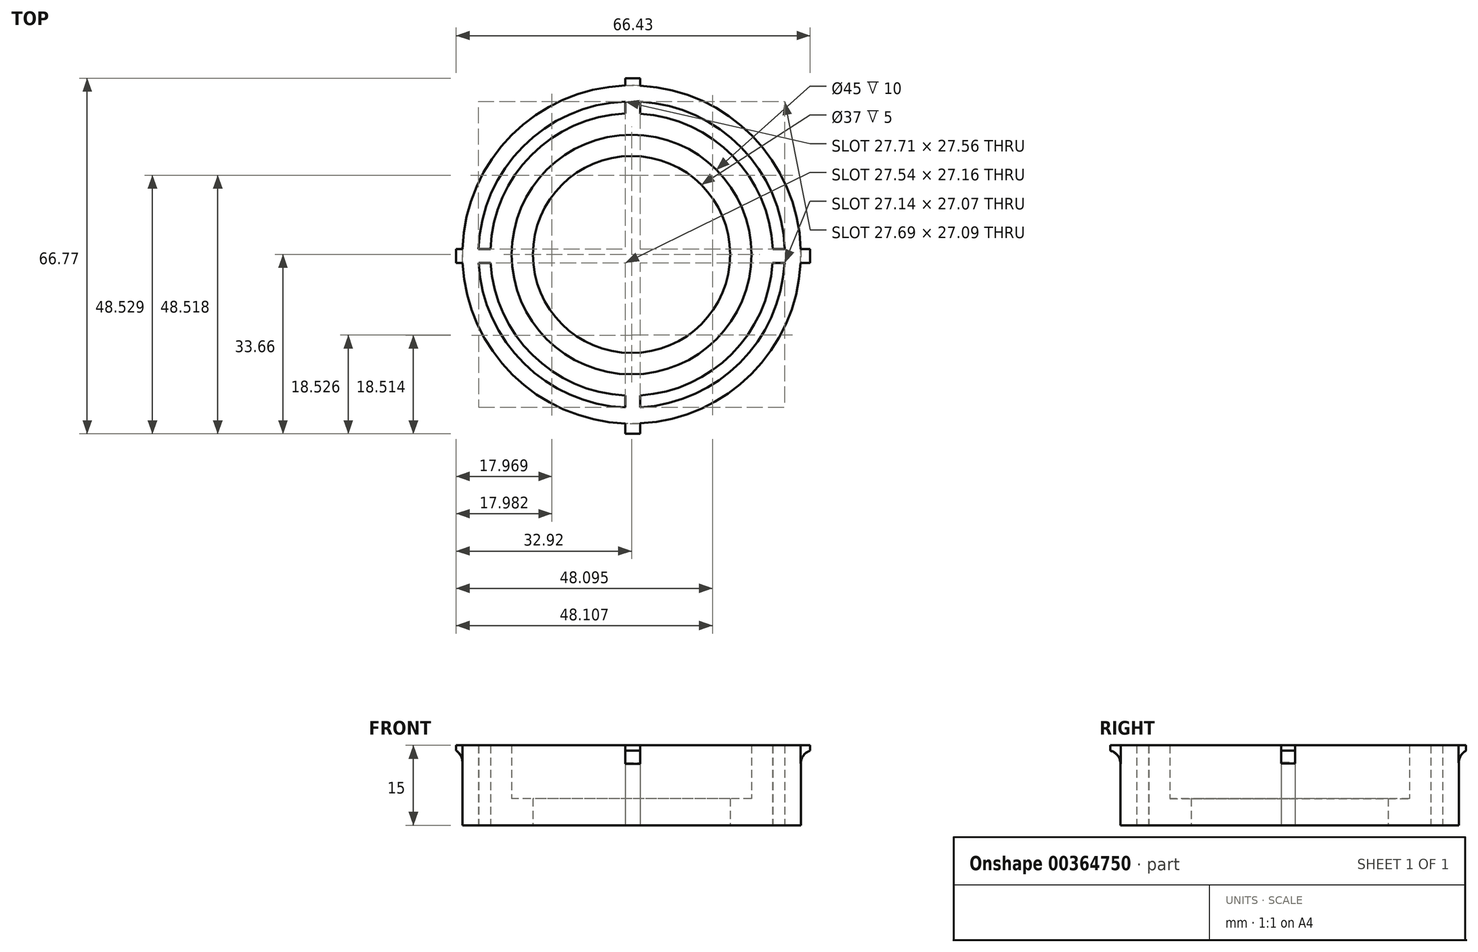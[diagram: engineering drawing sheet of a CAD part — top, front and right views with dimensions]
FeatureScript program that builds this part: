
annotation { "Feature Type Name" : "Feature", "Feature Type Description" : "" }
export const myFeature = defineFeature(function(context is Context, id is Id, definition is map)
    precondition{}
    {
        {
            var Q0;
            Q0=qCreatedBy(makeId("Top.planeOp"),FACE);
            var sketch = newSketch(context, id + "F0", { "sketchPlane" : qUnion([Q0])});
            skCircle(sketch, "E0", {"center": v(0, 0) * mm, "radius": 18.5 * mm});
            skCircle(sketch, "E1.0", {"center": v(0, 0) * mm, "radius": 22.5 * mm});
            skCircle(sketch, "E2.0", {"center": v(0, 0) * mm, "radius": 26.5 * mm});
            skLineSegment(sketch, "E3.bottom", {"start": v(-32.92, 1.01) * mm, "end": v(-24.48, 1.01) * mm});
            skLineSegment(sketch, "E3.top", {"start": v(-32.92, -1.56) * mm, "end": v(-24.48, -1.56) * mm});
            skLineSegment(sketch, "E3.left", {"start": v(-32.92, 1.01) * mm, "end": v(-32.92, -1.56) * mm});
            skLineSegment(sketch, "E3.right", {"start": v(-24.48, 1.01) * mm, "end": v(-24.48, -1.56) * mm});
            skLineSegment(sketch, "E4.bottom", {"start": v(-1.17, 33.11) * mm, "end": v(1.64, 33.11) * mm});
            skLineSegment(sketch, "E4.top", {"start": v(-1.17, 24.56) * mm, "end": v(1.64, 24.56) * mm});
            skLineSegment(sketch, "E4.left", {"start": v(-1.17, 33.11) * mm, "end": v(-1.17, 24.56) * mm});
            skLineSegment(sketch, "E4.right", {"start": v(1.64, 33.11) * mm, "end": v(1.64, 24.56) * mm});
            skLineSegment(sketch, "E5.bottom", {"start": v(33.5, -1.56) * mm, "end": v(24.13, -1.56) * mm});
            skLineSegment(sketch, "E5.top", {"start": v(33.5, 1.01) * mm, "end": v(24.13, 1.01) * mm});
            skLineSegment(sketch, "E5.left", {"start": v(33.5, -1.56) * mm, "end": v(33.5, 1.01) * mm});
            skLineSegment(sketch, "E5.right", {"start": v(24.13, -1.56) * mm, "end": v(24.13, 1.01) * mm});
            skLineSegment(sketch, "E6.bottom", {"start": v(-1.17, -25) * mm, "end": v(1.64, -25) * mm});
            skLineSegment(sketch, "E6.top", {"start": v(-1.17, -33.66) * mm, "end": v(1.64, -33.66) * mm});
            skLineSegment(sketch, "E6.left", {"start": v(-1.17, -25) * mm, "end": v(-1.17, -33.66) * mm});
            skLineSegment(sketch, "E6.right", {"start": v(1.64, -25) * mm, "end": v(1.64, -33.66) * mm});
            skCircle(sketch, "E7.0", {"center": v(0, 0) * mm, "radius": 31.75 * mm});
            skCircle(sketch, "E8.0", {"center": v(0, 0) * mm, "radius": 28.75 * mm});
            skCircle(sketch, "E9.0", {"center": v(0, 0) * mm, "radius": 34.75 * mm});
            skSolve(sketch);
        }
        {
            var Q0;
            Q0=makeQuery(id+"F0.imprint","IMPRINT",FACE,{"disambiguationData":[TD([[makeQuery(id+"F0.imprint","IMPRINT",EDGE,{"derivedFrom":sQuery(id+"F0.wireOp",EDGE,"E1.0")}),-1.0]])]});
            var Q1;
            {var subQ5=sQuery(id+"F0.wireOp",EDGE,"E6.bottom");Q1=makeQuery(id+"F0.imprint","IMPRINT",FACE,{"disambiguationData":[TD([[makeQuery(id+"F0.imprint","IMPRINT",EDGE,{"derivedFrom":subQ5}),-1.0]])]});}
            var Q2;
            {var subQ0=sQuery(id+"F0.wireOp",EDGE,"E6.left");var subQ1=sQuery(id+"F0.wireOp",EDGE,"E2.0");var subQ2=makeQuery(id+"F0.imprint","INTERSECT",VERTEX,{"derivedFrom":[subQ1,subQ0]});Q2=makeQuery(id+"F0.imprint","IMPRINT",FACE,{"disambiguationData":[TD([[makeQuery(id+"F0.imprint","IMPRINT",EDGE,{"disambiguationData":[TD([[subQ2,-1.0]])],"derivedFrom":subQ1}),-1.0]])]});}
            var Q3;
            {var subQ0=sQuery(id+"F0.wireOp",EDGE,"E7.0");var subQ1=sQuery(id+"F0.wireOp",EDGE,"E6.left");var subQ2=makeQuery(id+"F0.imprint","INTERSECT",VERTEX,{"derivedFrom":[subQ1,subQ0]});Q3=makeQuery(id+"F0.imprint","IMPRINT",FACE,{"disambiguationData":[TD([[makeQuery(id+"F0.imprint","IMPRINT",EDGE,{"disambiguationData":[TD([[subQ2,1.0]])],"derivedFrom":subQ1}),1.0]])]});}
            var Q4;
            {var subQ0=sQuery(id+"F0.wireOp",EDGE,"E7.0");var subQ1=sQuery(id+"F0.wireOp",EDGE,"E5.bottom");var subQ2=makeQuery(id+"F0.imprint","INTERSECT",VERTEX,{"derivedFrom":[subQ1,subQ0]});Q4=makeQuery(id+"F0.imprint","IMPRINT",FACE,{"disambiguationData":[TD([[makeQuery(id+"F0.imprint","IMPRINT",EDGE,{"disambiguationData":[TD([[subQ2,-1.0]])],"derivedFrom":subQ1}),1.0]])]});}
            var Q5;
            {var subQ0=sQuery(id+"F0.wireOp",EDGE,"E7.0");var subQ1=sQuery(id+"F0.wireOp",EDGE,"E5.bottom");var subQ2=makeQuery(id+"F0.imprint","INTERSECT",VERTEX,{"derivedFrom":[subQ1,subQ0]});Q5=makeQuery(id+"F0.imprint","IMPRINT",FACE,{"disambiguationData":[TD([[makeQuery(id+"F0.imprint","IMPRINT",EDGE,{"disambiguationData":[TD([[subQ2,-1.0]])],"derivedFrom":subQ1}),-1.0]])]});}
            var Q6;
            {var subQ0=sQuery(id+"F0.wireOp",EDGE,"E7.0");var subQ1=sQuery(id+"F0.wireOp",EDGE,"E4.right");var subQ2=makeQuery(id+"F0.imprint","INTERSECT",VERTEX,{"derivedFrom":[subQ1,subQ0]});Q6=makeQuery(id+"F0.imprint","IMPRINT",FACE,{"disambiguationData":[TD([[makeQuery(id+"F0.imprint","IMPRINT",EDGE,{"disambiguationData":[TD([[subQ2,-1.0]])],"derivedFrom":subQ1}),1.0]])]});}
            var Q7;
            {var subQ0=sQuery(id+"F0.wireOp",EDGE,"E5.top");var subQ1=sQuery(id+"F0.wireOp",EDGE,"E2.0");var subQ2=makeQuery(id+"F0.imprint","INTERSECT",VERTEX,{"derivedFrom":[subQ1,subQ0]});Q7=makeQuery(id+"F0.imprint","IMPRINT",FACE,{"disambiguationData":[TD([[makeQuery(id+"F0.imprint","IMPRINT",EDGE,{"disambiguationData":[TD([[subQ2,1.0]])],"derivedFrom":subQ1}),-1.0]])]});}
            var Q8;
            {var subQ5=sQuery(id+"F0.wireOp",EDGE,"E5.right");Q8=makeQuery(id+"F0.imprint","IMPRINT",FACE,{"disambiguationData":[TD([[makeQuery(id+"F0.imprint","IMPRINT",EDGE,{"derivedFrom":subQ5}),-1.0]])]});}
            var Q9;
            {var subQ5=sQuery(id+"F0.wireOp",EDGE,"E4.top");Q9=makeQuery(id+"F0.imprint","IMPRINT",FACE,{"disambiguationData":[TD([[makeQuery(id+"F0.imprint","IMPRINT",EDGE,{"derivedFrom":subQ5}),1.0]])]});}
            var Q10;
            {var subQ0=sQuery(id+"F0.wireOp",EDGE,"E4.right");var subQ1=sQuery(id+"F0.wireOp",EDGE,"E2.0");var subQ2=makeQuery(id+"F0.imprint","INTERSECT",VERTEX,{"derivedFrom":[subQ1,subQ0]});Q10=makeQuery(id+"F0.imprint","IMPRINT",FACE,{"disambiguationData":[TD([[makeQuery(id+"F0.imprint","IMPRINT",EDGE,{"disambiguationData":[TD([[subQ2,-1.0]])],"derivedFrom":subQ1}),-1.0]])]});}
            var Q11;
            {var subQ0=sQuery(id+"F0.wireOp",EDGE,"E7.0");var subQ1=sQuery(id+"F0.wireOp",EDGE,"E4.left");var subQ2=makeQuery(id+"F0.imprint","INTERSECT",VERTEX,{"derivedFrom":[subQ1,subQ0]});Q11=makeQuery(id+"F0.imprint","IMPRINT",FACE,{"disambiguationData":[TD([[makeQuery(id+"F0.imprint","IMPRINT",EDGE,{"disambiguationData":[TD([[subQ2,-1.0]])],"derivedFrom":subQ1}),1.0]])]});}
            var Q12;
            {var subQ0=sQuery(id+"F0.wireOp",EDGE,"E7.0");var subQ1=sQuery(id+"F0.wireOp",EDGE,"E3.bottom");var subQ2=makeQuery(id+"F0.imprint","INTERSECT",VERTEX,{"derivedFrom":[subQ1,subQ0]});Q12=makeQuery(id+"F0.imprint","IMPRINT",FACE,{"disambiguationData":[TD([[makeQuery(id+"F0.imprint","IMPRINT",EDGE,{"disambiguationData":[TD([[subQ2,-1.0]])],"derivedFrom":subQ1}),1.0]])]});}
            var Q13;
            {var subQ5=sQuery(id+"F0.wireOp",EDGE,"E3.right");Q13=makeQuery(id+"F0.imprint","IMPRINT",FACE,{"disambiguationData":[TD([[makeQuery(id+"F0.imprint","IMPRINT",EDGE,{"derivedFrom":subQ5}),-1.0]])]});}
            var Q14;
            {var subQ0=sQuery(id+"F0.wireOp",EDGE,"E3.bottom");var subQ1=sQuery(id+"F0.wireOp",EDGE,"E2.0");var subQ2=makeQuery(id+"F0.imprint","INTERSECT",VERTEX,{"derivedFrom":[subQ1,subQ0]});Q14=makeQuery(id+"F0.imprint","IMPRINT",FACE,{"disambiguationData":[TD([[makeQuery(id+"F0.imprint","IMPRINT",EDGE,{"disambiguationData":[TD([[subQ2,-1.0]])],"derivedFrom":subQ1}),-1.0]])]});}
            var Q15;
            {var subQ0=sQuery(id+"F0.wireOp",EDGE,"E7.0");var subQ1=sQuery(id+"F0.wireOp",EDGE,"E3.bottom");var subQ2=makeQuery(id+"F0.imprint","INTERSECT",VERTEX,{"derivedFrom":[subQ1,subQ0]});Q15=makeQuery(id+"F0.imprint","IMPRINT",FACE,{"disambiguationData":[TD([[makeQuery(id+"F0.imprint","IMPRINT",EDGE,{"disambiguationData":[TD([[subQ2,-1.0]])],"derivedFrom":subQ1}),-1.0]])]});}
            var Q16;
            {var subQ0=sQuery(id+"F0.wireOp",EDGE,"E7.0");var subQ1=sQuery(id+"F0.wireOp",EDGE,"E3.top");var subQ2=makeQuery(id+"F0.imprint","INTERSECT",VERTEX,{"derivedFrom":[subQ1,subQ0]});Q16=makeQuery(id+"F0.imprint","IMPRINT",FACE,{"disambiguationData":[TD([[makeQuery(id+"F0.imprint","IMPRINT",EDGE,{"disambiguationData":[TD([[subQ2,-1.0]])],"derivedFrom":subQ1}),-1.0]])]});}
            var Q17;
            {var subQ0=sQuery(id+"F0.wireOp",EDGE,"E5.left");Q17=makeQuery(id+"F0.imprint","IMPRINT",FACE,{"disambiguationData":[TD([[makeQuery(id+"F0.imprint","IMPRINT",EDGE,{"derivedFrom":subQ0}),1.0]])]});}
            var Q18;
            {var subQ0=sQuery(id+"F0.wireOp",EDGE,"E4.bottom");Q18=makeQuery(id+"F0.imprint","IMPRINT",FACE,{"disambiguationData":[TD([[makeQuery(id+"F0.imprint","IMPRINT",EDGE,{"derivedFrom":subQ0}),-1.0]])]});}
            var Q19;
            {var subQ0=sQuery(id+"F0.wireOp",EDGE,"E3.left");Q19=makeQuery(id+"F0.imprint","IMPRINT",FACE,{"disambiguationData":[TD([[makeQuery(id+"F0.imprint","IMPRINT",EDGE,{"derivedFrom":subQ0}),1.0]])]});}
            var Q20;
            {var subQ0=sQuery(id+"F0.wireOp",EDGE,"E6.top");Q20=makeQuery(id+"F0.imprint","IMPRINT",FACE,{"disambiguationData":[TD([[makeQuery(id+"F0.imprint","IMPRINT",EDGE,{"derivedFrom":subQ0}),1.0]])]});}
            extrude(context, id + "F1", {"entities" : qUnion([Q0, Q1, Q2, Q3, Q4, Q5, Q6, Q7, Q8, Q9, Q10, Q11, Q12, Q13, Q14, Q15, Q16, Q17, Q18, Q19, Q20]), "depth" : 15 * mm});
        }
        {
            var Q0;
            Q0=makeQuery(id+"F0.imprint","IMPRINT",FACE,{"disambiguationData":[TD([[makeQuery(id+"F0.imprint","IMPRINT",EDGE,{"derivedFrom":sQuery(id+"F0.wireOp",EDGE,"E0")}),-1.0]])]});
            extrude(context, id + "F2", {"entities" : qUnion([Q0]), "operationType" : NewBodyOperationType.ADD, "depth" : 5 * mm});
        }
        {
            var Q0;
            {var subQ0=sQuery(id+"F0.wireOp",EDGE,"E3.left");Q0=makeQuery(id+"F0.imprint","IMPRINT",FACE,{"disambiguationData":[TD([[makeQuery(id+"F0.imprint","IMPRINT",EDGE,{"derivedFrom":subQ0}),1.0]])]});}
            var Q1;
            {var subQ0=sQuery(id+"F0.wireOp",EDGE,"E6.top");Q1=makeQuery(id+"F0.imprint","IMPRINT",FACE,{"disambiguationData":[TD([[makeQuery(id+"F0.imprint","IMPRINT",EDGE,{"derivedFrom":subQ0}),1.0]])]});}
            var Q2;
            {var subQ0=sQuery(id+"F0.wireOp",EDGE,"E4.bottom");Q2=makeQuery(id+"F0.imprint","IMPRINT",FACE,{"disambiguationData":[TD([[makeQuery(id+"F0.imprint","IMPRINT",EDGE,{"derivedFrom":subQ0}),-1.0]])]});}
            var Q3;
            {var subQ0=sQuery(id+"F0.wireOp",EDGE,"E5.left");Q3=makeQuery(id+"F0.imprint","IMPRINT",FACE,{"disambiguationData":[TD([[makeQuery(id+"F0.imprint","IMPRINT",EDGE,{"derivedFrom":subQ0}),1.0]])]});}
            extrude(context, id + "F3", {"entities" : qUnion([Q0, Q1, Q2, Q3]), "operationType" : NewBodyOperationType.REMOVE, "depth" : 14 * mm});
        }
        {
            var Q0;
            {var subQ0=sQuery(id+"F0.wireOp",EDGE,"E7.0");Q0=makeQuery(id+"F3.boolean.opBoolean","COPY",EDGE,{"derivedFrom":makeQuery(id+"F3.opExtrude","CAP_EDGE",EDGE,{"disambiguationData":[OSD([subQ0]),TDD([makeQuery(id+"F0.imprint","IMPRINT",EDGE,{"disambiguationData":[TD([[makeQuery(id+"F0.imprint","INTERSECT",VERTEX,{"derivedFrom":[sQuery(id+"F0.wireOp",EDGE,"E6.left"),subQ0]}),-1.0]])],"derivedFrom":subQ0})])],"isStart":false})});}
            var Q1;
            {var subQ0=sQuery(id+"F0.wireOp",EDGE,"E7.0");Q1=makeQuery(id+"F3.boolean.opBoolean","COPY",EDGE,{"derivedFrom":makeQuery(id+"F3.opExtrude","CAP_EDGE",EDGE,{"disambiguationData":[OSD([subQ0]),TDD([makeQuery(id+"F0.imprint","IMPRINT",EDGE,{"disambiguationData":[TD([[makeQuery(id+"F0.imprint","INTERSECT",VERTEX,{"derivedFrom":[sQuery(id+"F0.wireOp",EDGE,"E5.bottom"),subQ0]}),-1.0]])],"derivedFrom":subQ0})])],"isStart":false})});}
            var Q2;
            {var subQ0=sQuery(id+"F0.wireOp",EDGE,"E7.0");Q2=makeQuery(id+"F3.boolean.opBoolean","COPY",EDGE,{"derivedFrom":makeQuery(id+"F3.opExtrude","CAP_EDGE",EDGE,{"disambiguationData":[OSD([subQ0]),TDD([makeQuery(id+"F0.imprint","IMPRINT",EDGE,{"disambiguationData":[TD([[makeQuery(id+"F0.imprint","INTERSECT",VERTEX,{"derivedFrom":[sQuery(id+"F0.wireOp",EDGE,"E4.left"),subQ0]}),1.0]])],"derivedFrom":subQ0})])],"isStart":false})});}
            var Q3;
            {var subQ0=sQuery(id+"F0.wireOp",EDGE,"E7.0");Q3=makeQuery(id+"F3.boolean.opBoolean","COPY",EDGE,{"derivedFrom":makeQuery(id+"F3.opExtrude","CAP_EDGE",EDGE,{"disambiguationData":[OSD([subQ0]),TDD([makeQuery(id+"F0.imprint","IMPRINT",EDGE,{"disambiguationData":[TD([[makeQuery(id+"F0.imprint","INTERSECT",VERTEX,{"derivedFrom":[sQuery(id+"F0.wireOp",EDGE,"E3.bottom"),subQ0]}),-1.0]])],"derivedFrom":subQ0})])],"isStart":false})});}
            fillet(context, id + "F4", {"entities" : qUnion([Q0, Q1, Q2, Q3]), "radius" : 2.54 * mm, "tangentPropagation" : true, "allowEdgeOverflow" : false});
        }
    });
